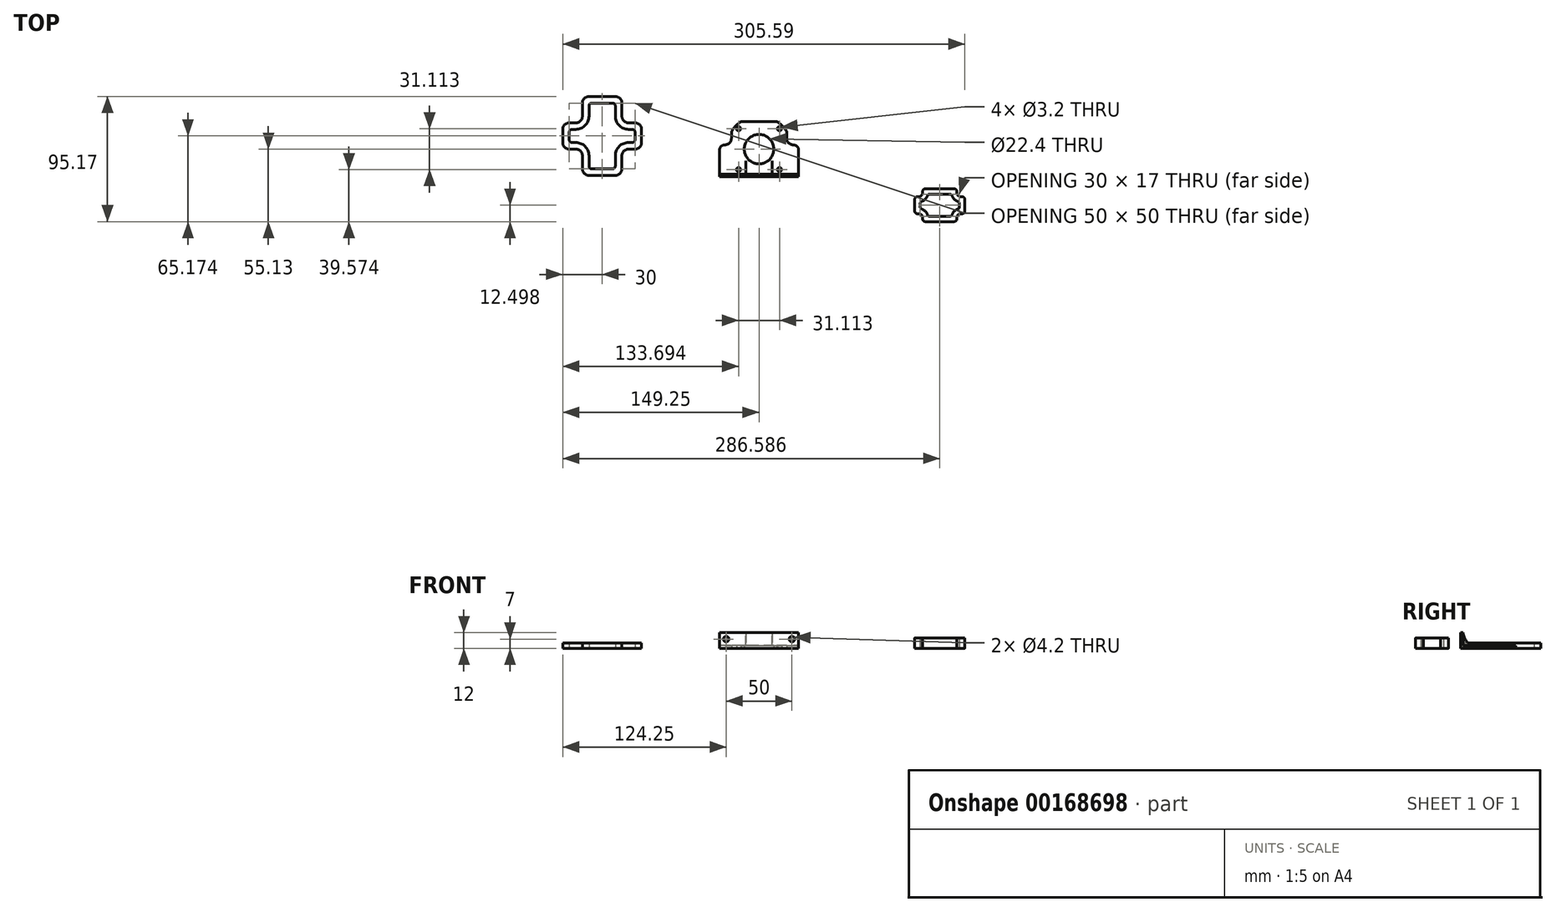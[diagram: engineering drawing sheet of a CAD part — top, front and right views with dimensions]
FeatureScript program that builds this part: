
annotation { "Feature Type Name" : "Feature", "Feature Type Description" : "" }
export const myFeature = defineFeature(function(context is Context, id is Id, definition is map)
    precondition{}
    {
        {
            var Q0;
            Q0=qCreatedBy(makeId("Top.planeOp"),FACE);
            var sketch = newSketch(context, id + "F0", { "sketchPlane" : qUnion([Q0])});
            skCircle(sketch, "E0", {"center": v(0, 0) * mm, "radius": 11.2 * mm});
            skLineSegment(sketch, "E1.bottom", {"start": v(-21, 21) * mm, "end": v(21, 21) * mm});
            skLineSegment(sketch, "E1.top", {"start": v(-21, -21) * mm, "end": v(21, -21) * mm});
            skLineSegment(sketch, "E1.left", {"start": v(-21, 21) * mm, "end": v(-21, 8.3) * mm});
            skLineSegment(sketch, "E1.right", {"start": v(21, 21) * mm, "end": v(21, 8.3) * mm});
            skLineSegment(sketch, "E2", {"start": v(-21, 21) * mm, "end": v(21, -21) * mm, "construction": true});
            skLineSegment(sketch, "E3", {"start": v(-21, -21) * mm, "end": v(21, 21) * mm, "construction": true});
            skCircle(sketch, "E4", {"center": v(0, 0) * mm, "radius": 22 * mm, "construction": true});
            skCircle(sketch, "E5", {"center": v(-15.56, 15.56) * mm, "radius": 1.6 * mm});
            skCircle(sketch, "E6", {"center": v(15.56, 15.56) * mm, "radius": 1.6 * mm});
            skCircle(sketch, "E7", {"center": v(-15.56, -15.56) * mm, "radius": 1.6 * mm});
            skCircle(sketch, "E8", {"center": v(15.56, -15.56) * mm, "radius": 1.6 * mm});
            skLineSegment(sketch, "E9.bottom", {"start": v(-30, -21) * mm, "end": v(30, -21) * mm});
            skLineSegment(sketch, "E9.top", {"start": v(-30, -19) * mm, "end": v(30, -19) * mm});
            skLineSegment(sketch, "E9.left", {"start": v(-30, -19) * mm, "end": v(-30, -21) * mm});
            skLineSegment(sketch, "E9.right", {"start": v(30, -19) * mm, "end": v(30, -21) * mm});
            skLineSegment(sketch, "E10.bottom", {"start": v(-30, -19) * mm, "end": v(-21, -19) * mm});
            skLineSegment(sketch, "E10.top", {"start": v(-26, 3.3) * mm, "end": v(-26, 3.3) * mm});
            skLineSegment(sketch, "E10.left", {"start": v(-30, -19) * mm, "end": v(-30, -0.7) * mm});
            skLineSegment(sketch, "E10.right", {"start": v(-21, -19) * mm, "end": v(-21, 0) * mm});
            skLineSegment(sketch, "E11.bottom", {"start": v(30, -19) * mm, "end": v(21, -19) * mm});
            skLineSegment(sketch, "E11.top", {"start": v(26, 3.3) * mm, "end": v(26, 3.3) * mm});
            skLineSegment(sketch, "E11.left", {"start": v(30, -19) * mm, "end": v(30, -0.7) * mm});
            skLineSegment(sketch, "E11.right", {"start": v(21, -19) * mm, "end": v(21, 0) * mm});
            skPoint(sketch, "E12.newPointA", {"position": v(-21, 3.3) * mm});
            skPoint(sketch, "E12.newPointB", {"position": v(-21, -14.42) * mm});
            skArc(sketch, "E12.filletArc", {"start": v(-26, 3.3) * mm, "mid": v(-22.46, 4.76) * mm, "end": v(-21, 8.3) * mm});
            skPoint(sketch, "E13.newPointA", {"position": v(21, 3.3) * mm});
            skPoint(sketch, "E13.newPointB", {"position": v(21, -14.42) * mm});
            skArc(sketch, "E13.filletArc", {"start": v(21, 8.3) * mm, "mid": v(22.46, 4.76) * mm, "end": v(26, 3.3) * mm});
            skPoint(sketch, "E14.visualSharp", {"position": v(-30, 3.3) * mm});
            skArc(sketch, "E14.filletArc", {"start": v(-26, 3.3) * mm, "mid": v(-28.83, 2.12) * mm, "end": v(-30, -0.7) * mm});
            skPoint(sketch, "E15.visualSharp", {"position": v(30, 3.3) * mm});
            skArc(sketch, "E15.filletArc", {"start": v(30, -0.7) * mm, "mid": v(28.83, 2.12) * mm, "end": v(26, 3.3) * mm});
            skArc(sketch, "E16", {"start": v(-21, 13.56) * mm, "mid": v(-17.68, 17.68) * mm, "end": v(-13.56, 21) * mm});
            skArc(sketch, "E17.MirrorCS", {"start": v(21, 13.56) * mm, "mid": v(17.68, 17.68) * mm, "end": v(13.56, 21) * mm});
            skSolve(sketch);
        }
        {
            var Q0;
            Q0=makeQuery(id+"F0.imprint","IMPRINT",FACE,{"disambiguationData":[TD([[makeQuery(id+"F0.imprint","IMPRINT",EDGE,{"derivedFrom":sQuery(id+"F0.wireOp",EDGE,"E0")}),-1.0]])]});
            extrude(context, id + "F1", {"entities" : qUnion([Q0]), "depth" : 2 * mm});
        }
        {
            var Q0;
            Q0=makeQuery(id+"F0.imprint","IMPRINT",FACE,{"disambiguationData":[TD([[makeQuery(id+"F0.imprint","IMPRINT",EDGE,{"derivedFrom":sQuery(id+"F0.wireOp",EDGE,"E9.top")}),-1.0]])]});
            extrude(context, id + "F2", {"entities" : qUnion([Q0]), "operationType" : NewBodyOperationType.ADD, "depth" : 12 * mm});
        }
        {
            var Q0;
            Q0=makeQuery(id+"F2.opExtrude","SWEPT_FACE",FACE,{"disambiguationData":[OSD([sQuery(id+"F0.wireOp",EDGE,"E9.top"),sQuery(id+"F0.wireOp",EDGE,"E10.bottom"),sQuery(id+"F0.wireOp",EDGE,"E11.bottom")])]});
            var sketch = newSketch(context, id + "F3", { "sketchPlane" : qUnion([Q0])});
            skLineSegment(sketch, "E18", {"start": v(20, 2) * mm, "end": v(20, 12) * mm});
            skCircle(sketch, "E19", {"center": v(25, 7) * mm, "radius": 2.1 * mm});
            skPoint(sketch, "E19.centerSnap0", {"position": v(20, 7) * mm});
            skCircle(sketch, "E20", {"center": v(-25, 7) * mm, "radius": 2.1 * mm});
            skSolve(sketch);
        }
        {
            var Q0;
            Q0=makeQuery(id+"F2.boolean.opBoolean","MERGE",FACE,{"derivedFrom":[makeQuery(id+"F1.opExtrude","SWEPT_FACE",FACE,{"disambiguationData":[OSD([sQuery(id+"F0.wireOp",EDGE,"E10.left")])]}),makeQuery(id+"F2.opExtrude","SWEPT_FACE",FACE,{"disambiguationData":[OSD([sQuery(id+"F0.wireOp",EDGE,"E9.left")])]})]});
            var sketch = newSketch(context, id + "F4", { "sketchPlane" : qUnion([Q0])});
            skLineSegment(sketch, "E21", {"start": v(0.7, 2) * mm, "end": v(9, 2) * mm});
            skLineSegment(sketch, "E22", {"start": v(19, 12) * mm, "end": v(19, 12) * mm});
            skPoint(sketch, "E23.visualSharp", {"position": v(19, 2) * mm});
            skArc(sketch, "E23.filletArc", {"start": v(9, 2) * mm, "mid": v(16.07, 4.93) * mm, "end": v(19, 12) * mm});
            skSolve(sketch);
        }
        {
            var Q0;
            Q0 = qSketchRegion(id + "F4", true);
            var Q1;
            {var subQ0=sQuery(id+"F4.wireOp",EDGE,"E23.filletArc");Q1=makeQuery(id+"F4.imprint","IMPRINT",FACE,{"disambiguationData":[TD([[makeQuery(id+"F4.imprint","IMPRINT",EDGE,{"derivedFrom":subQ0}),-1.0]])]});}
            extrude(context, id + "F5", {"entities" : qUnion([Q0, Q1]), "operationType" : NewBodyOperationType.ADD, "oppositeDirection" : true, "depth" : 40 * mm});
        }
        {
            var Q0;
            {var subQ0=sQuery(id+"F4.wireOp",EDGE,"E23.filletArc");Q0=makeQuery(id+"F4.imprint","IMPRINT",FACE,{"disambiguationData":[TD([[makeQuery(id+"F4.imprint","IMPRINT",EDGE,{"derivedFrom":subQ0}),-1.0]])]});}
            extrude(context, id + "F6", {"entities" : qUnion([Q0]), "operationType" : NewBodyOperationType.REMOVE, "oppositeDirection" : true, "depth" : 20 * mm});
        }
        {
            var Q0;
            Q0=makeQuery(id+"F3.imprint","IMPRINT",FACE,{"disambiguationData":[TD([[makeQuery(id+"F3.imprint","IMPRINT",EDGE,{"derivedFrom":sQuery(id+"F3.wireOp",EDGE,"E20")}),1.0]])]});
            var Q1;
            Q1=makeQuery(id+"F3.imprint","IMPRINT",FACE,{"disambiguationData":[TD([[makeQuery(id+"F3.imprint","IMPRINT",EDGE,{"derivedFrom":sQuery(id+"F3.wireOp",EDGE,"E19")}),1.0]])]});
            extrude(context, id + "F7", {"entities" : qUnion([Q0, Q1]), "operationType" : NewBodyOperationType.REMOVE, "oppositeDirection" : true, "depth" : 25 * mm});
        }
        {
            var Q0;
            Q0=makeQuery(id+"F0.imprint","IMPRINT",FACE,{"disambiguationData":[TD([[makeQuery(id+"F0.imprint","IMPRINT",EDGE,{"derivedFrom":sQuery(id+"F0.wireOp",EDGE,"E0")}),1.0]])]});
            extrude(context, id + "F8", {"entities" : qUnion([Q0]), "operationType" : NewBodyOperationType.REMOVE, "depth" : 25 * mm});
        }
        {
            var Q0;
            Q0=makeQuery(id+"F1.opExtrude","CAP_EDGE",EDGE,{"disambiguationData":[OSD([sQuery(id+"F0.wireOp",EDGE,"E9.top"),sQuery(id+"F0.wireOp",EDGE,"E10.bottom"),sQuery(id+"F0.wireOp",EDGE,"E11.bottom")])],"isStart":false});
            var Q1;
            Q1=makeQuery(id+"F6.boolean.opBoolean","COPY",EDGE,{"derivedFrom":makeQuery(id+"F6.opExtrude","SWEPT_EDGE",EDGE,{"disambiguationData":[OSD([sQuery(id+"F0.wireOp",EDGE,"E9.left"),sQuery(id+"F0.wireOp",EDGE,"E10.bottom"),sQuery(id+"F0.wireOp",EDGE,"E10.left")])]})});
            fillet(context, id + "F9", {"entities" : qUnion([Q0, Q1]), "radius" : 1 * mm, "tangentPropagation" : true, "allowEdgeOverflow" : false});
        }
        {
            var Q0;
            Q0=qCreatedBy(makeId("Top.planeOp"),FACE);
            var sketch = newSketch(context, id + "F10", { "sketchPlane" : qUnion([Q0])});
            skLineSegment(sketch, "E24.bottom", {"start": v(-109.25, -19.96) * mm, "end": v(-129.25, -19.96) * mm});
            skLineSegment(sketch, "E24.top", {"start": v(-109.25, 40.04) * mm, "end": v(-129.25, 40.04) * mm});
            skLineSegment(sketch, "E24.left", {"start": v(-89.25, 5.04) * mm, "end": v(-89.25, 15.04) * mm});
            skLineSegment(sketch, "E24.right", {"start": v(-149.25, 5.04) * mm, "end": v(-149.25, 15.04) * mm});
            skPoint(sketch, "E24.middle", {"position": v(-119.25, 10.04) * mm});
            skLineSegment(sketch, "E25.0", {"start": v(-139.25, 20.04) * mm, "end": v(-144.25, 20.04) * mm});
            skLineSegment(sketch, "E26.0", {"start": v(-139.25, 0.04) * mm, "end": v(-144.25, 0.04) * mm});
            skLineSegment(sketch, "E27.0", {"start": v(-134.25, -14.96) * mm, "end": v(-134.25, -4.96) * mm});
            skLineSegment(sketch, "E28.0", {"start": v(-104.25, -14.96) * mm, "end": v(-104.25, -4.96) * mm});
            skArc(sketch, "E29.filletArc", {"start": v(-144.25, 20.04) * mm, "mid": v(-147.79, 18.58) * mm, "end": v(-149.25, 15.04) * mm});
            skArc(sketch, "E30.filletArc", {"start": v(-149.25, 5.04) * mm, "mid": v(-147.79, 1.5) * mm, "end": v(-144.25, 0.04) * mm});
            skArc(sketch, "E31.filletArc", {"start": v(-134.25, -4.96) * mm, "mid": v(-135.71, -1.42) * mm, "end": v(-139.25, 0.04) * mm});
            skPoint(sketch, "E32.newPointB", {"position": v(-149.25, -19.96) * mm});
            skArc(sketch, "E32.filletArc", {"start": v(-134.25, -14.96) * mm, "mid": v(-132.79, -18.5) * mm, "end": v(-129.25, -19.96) * mm});
            skPoint(sketch, "E33.newPointA", {"position": v(-89.25, -19.96) * mm});
            skArc(sketch, "E33.filletArc", {"start": v(-109.25, -19.96) * mm, "mid": v(-105.71, -18.5) * mm, "end": v(-104.25, -14.96) * mm});
            skLineSegment(sketch, "E34", {"start": v(-134.25, 35.04) * mm, "end": v(-134.25, 25.04) * mm});
            skPoint(sketch, "E34.startSnap0", {"position": v(-119.25, 40.04) * mm});
            skLineSegment(sketch, "E35", {"start": v(-94.25, 0.04) * mm, "end": v(-99.25, 0.04) * mm});
            skArc(sketch, "E36.filletArc", {"start": v(-139.25, 20.04) * mm, "mid": v(-135.71, 21.5) * mm, "end": v(-134.25, 25.04) * mm});
            skPoint(sketch, "E37.newPointB", {"position": v(-89.25, 40.04) * mm});
            skArc(sketch, "E37.filletArc", {"start": v(-104.25, 35.04) * mm, "mid": v(-105.71, 38.58) * mm, "end": v(-109.25, 40.04) * mm});
            skPoint(sketch, "E38.newPointA", {"position": v(-134.25, 40.04) * mm});
            skPoint(sketch, "E38.newPointB", {"position": v(-149.25, 40.04) * mm});
            skArc(sketch, "E38.filletArc", {"start": v(-129.25, 40.04) * mm, "mid": v(-132.79, 38.58) * mm, "end": v(-134.25, 35.04) * mm});
            skPoint(sketch, "E39.newPointA", {"position": v(-89.25, 0.04) * mm});
            skArc(sketch, "E39.filletArc", {"start": v(-94.25, 0.04) * mm, "mid": v(-90.71, 1.5) * mm, "end": v(-89.25, 5.04) * mm});
            skArc(sketch, "E40.filletArc", {"start": v(-99.25, 0.04) * mm, "mid": v(-102.79, -1.42) * mm, "end": v(-104.25, -4.96) * mm});
            skLineSegment(sketch, "E41", {"start": v(-104.25, 35.04) * mm, "end": v(-104.25, 25.04) * mm});
            skLineSegment(sketch, "E42", {"start": v(-94.25, 20.04) * mm, "end": v(-99.25, 20.04) * mm});
            skArc(sketch, "E43.filletArc", {"start": v(-104.25, 25.04) * mm, "mid": v(-102.79, 21.5) * mm, "end": v(-99.25, 20.04) * mm});
            skPoint(sketch, "E44.newPointB", {"position": v(-89.25, 20.04) * mm});
            skArc(sketch, "E44.filletArc", {"start": v(-89.25, 15.04) * mm, "mid": v(-90.71, 18.58) * mm, "end": v(-94.25, 20.04) * mm});
            skLineSegment(sketch, "E45", {"start": v(-129.25, 33.04) * mm, "end": v(-129.25, 25.04) * mm});
            skLineSegment(sketch, "E46", {"start": v(-139.25, 15.04) * mm, "end": v(-142.25, 15.04) * mm});
            skLineSegment(sketch, "E47", {"start": v(-144.25, 13.04) * mm, "end": v(-144.25, 7.04) * mm});
            skLineSegment(sketch, "E48", {"start": v(-139.25, 5.04) * mm, "end": v(-142.25, 5.04) * mm});
            skLineSegment(sketch, "E49", {"start": v(-129.25, -4.96) * mm, "end": v(-129.25, -12.96) * mm});
            skLineSegment(sketch, "E50", {"start": v(-127.25, -14.96) * mm, "end": v(-111.25, -14.96) * mm});
            skLineSegment(sketch, "E51", {"start": v(-109.25, -4.96) * mm, "end": v(-109.25, -12.96) * mm});
            skLineSegment(sketch, "E52", {"start": v(-99.25, 5.04) * mm, "end": v(-96.25, 5.04) * mm});
            skLineSegment(sketch, "E53", {"start": v(-94.25, 13.04) * mm, "end": v(-94.25, 7.04) * mm});
            skLineSegment(sketch, "E54", {"start": v(-96.25, 15.04) * mm, "end": v(-99.25, 15.04) * mm});
            skLineSegment(sketch, "E55", {"start": v(-109.25, 25.04) * mm, "end": v(-109.25, 33.04) * mm});
            skLineSegment(sketch, "E56", {"start": v(-127.25, 35.04) * mm, "end": v(-111.25, 35.04) * mm});
            skPoint(sketch, "E57.visualSharp", {"position": v(-129.25, 15.04) * mm});
            skArc(sketch, "E57.filletArc", {"start": v(-139.25, 15.04) * mm, "mid": v(-132.18, 17.97) * mm, "end": v(-129.25, 25.04) * mm});
            skPoint(sketch, "E58.visualSharp", {"position": v(-129.25, 5.04) * mm});
            skArc(sketch, "E58.filletArc", {"start": v(-129.25, -4.96) * mm, "mid": v(-132.18, 2.12) * mm, "end": v(-139.25, 5.04) * mm});
            skPoint(sketch, "E59.visualSharp", {"position": v(-109.25, 5.04) * mm});
            skArc(sketch, "E59.filletArc", {"start": v(-99.25, 5.04) * mm, "mid": v(-106.32, 2.12) * mm, "end": v(-109.25, -4.96) * mm});
            skPoint(sketch, "E60.visualSharp", {"position": v(-109.25, 15.04) * mm});
            skArc(sketch, "E60.filletArc", {"start": v(-109.25, 25.04) * mm, "mid": v(-106.32, 17.97) * mm, "end": v(-99.25, 15.04) * mm});
            skArc(sketch, "E61.filletArc", {"start": v(-127.25, 35.04) * mm, "mid": v(-128.66, 34.46) * mm, "end": v(-129.25, 33.04) * mm});
            skArc(sketch, "E62.filletArc", {"start": v(-109.25, 33.04) * mm, "mid": v(-109.84, 34.46) * mm, "end": v(-111.25, 35.04) * mm});
            skArc(sketch, "E63.filletArc", {"start": v(-94.25, 13.04) * mm, "mid": v(-94.84, 14.46) * mm, "end": v(-96.25, 15.04) * mm});
            skArc(sketch, "E64.filletArc", {"start": v(-96.25, 5.04) * mm, "mid": v(-94.84, 5.63) * mm, "end": v(-94.25, 7.04) * mm});
            skArc(sketch, "E65.filletArc", {"start": v(-129.25, -12.96) * mm, "mid": v(-128.66, -14.37) * mm, "end": v(-127.25, -14.96) * mm});
            skArc(sketch, "E66.filletArc", {"start": v(-111.25, -14.96) * mm, "mid": v(-109.84, -14.37) * mm, "end": v(-109.25, -12.96) * mm});
            skArc(sketch, "E67.filletArc", {"start": v(-144.25, 7.04) * mm, "mid": v(-143.66, 5.63) * mm, "end": v(-142.25, 5.04) * mm});
            skArc(sketch, "E68.filletArc", {"start": v(-142.25, 15.04) * mm, "mid": v(-143.66, 14.46) * mm, "end": v(-144.25, 13.04) * mm});
            skLineSegment(sketch, "E69.bottom", {"start": v(121.34, -33.13) * mm, "end": v(153.34, -33.13) * mm, "construction": true});
            skLineSegment(sketch, "E69.top", {"start": v(121.34, -52.13) * mm, "end": v(153.34, -52.13) * mm, "construction": true});
            skLineSegment(sketch, "E69.left", {"start": v(121.34, -33.13) * mm, "end": v(121.34, -52.13) * mm, "construction": true});
            skLineSegment(sketch, "E69.right", {"start": v(153.34, -33.13) * mm, "end": v(153.34, -52.13) * mm, "construction": true});
            skCircle(sketch, "E70", {"center": v(121.34, -33.13) * mm, "radius": 3 * mm});
            skCircle(sketch, "E71", {"center": v(121.34, -52.13) * mm, "radius": 3 * mm});
            skCircle(sketch, "E72", {"center": v(153.34, -33.13) * mm, "radius": 3 * mm});
            skCircle(sketch, "E73", {"center": v(153.34, -52.13) * mm, "radius": 3 * mm});
            skLineSegment(sketch, "E74", {"start": v(118.34, -33.13) * mm, "end": v(118.34, -52.13) * mm});
            skLineSegment(sketch, "E75", {"start": v(121.34, -55.13) * mm, "end": v(153.34, -55.13) * mm});
            skLineSegment(sketch, "E76", {"start": v(156.34, -52.13) * mm, "end": v(156.34, -33.13) * mm});
            skLineSegment(sketch, "E77", {"start": v(153.34, -30.13) * mm, "end": v(121.34, -30.13) * mm});
            skLineSegment(sketch, "E78", {"start": v(121.34, -36.13) * mm, "end": v(118.34, -36.13) * mm});
            skLineSegment(sketch, "E79", {"start": v(121.34, -49.13) * mm, "end": v(118.34, -49.13) * mm});
            skLineSegment(sketch, "E80", {"start": v(124.34, -52.13) * mm, "end": v(124.34, -55.13) * mm});
            skLineSegment(sketch, "E81", {"start": v(150.34, -52.13) * mm, "end": v(150.34, -55.13) * mm});
            skLineSegment(sketch, "E82", {"start": v(153.34, -49.13) * mm, "end": v(156.34, -49.13) * mm});
            skLineSegment(sketch, "E83", {"start": v(153.34, -36.13) * mm, "end": v(156.34, -36.13) * mm});
            skLineSegment(sketch, "E84", {"start": v(150.34, -33.13) * mm, "end": v(150.34, -30.13) * mm});
            skCircle(sketch, "E85", {"center": v(121.34, -52.13) * mm, "radius": 7 * mm});
            skCircle(sketch, "E86", {"center": v(121.34, -33.13) * mm, "radius": 7 * mm});
            skCircle(sketch, "E87", {"center": v(153.34, -33.13) * mm, "radius": 7 * mm});
            skCircle(sketch, "E88", {"center": v(153.34, -52.13) * mm, "radius": 7 * mm});
            skLineSegment(sketch, "E89.0", {"start": v(122.34, -33.13) * mm, "end": v(122.34, -52.13) * mm});
            skLineSegment(sketch, "E90.0", {"start": v(152.34, -52.13) * mm, "end": v(152.34, -33.13) * mm});
            skLineSegment(sketch, "E91.0", {"start": v(153.34, -34.13) * mm, "end": v(121.34, -34.13) * mm});
            skLineSegment(sketch, "E92.0", {"start": v(121.34, -51.13) * mm, "end": v(153.34, -51.13) * mm});
            skLineSegment(sketch, "E93", {"start": v(124.34, -33.13) * mm, "end": v(124.34, -30.13) * mm});
            skSolve(sketch);
        }
        {
            var Q0;
            Q0=makeQuery(id+"F10.imprint","IMPRINT",FACE,{"disambiguationData":[TD([[makeQuery(id+"F10.imprint","IMPRINT",EDGE,{"derivedFrom":sQuery(id+"F10.wireOp",EDGE,"E24.bottom")}),-1.0]])]});
            extrude(context, id + "F11", {"entities" : qUnion([Q0]), "depth" : 4 * mm});
        }
        {
            var Q0;
            {var subQ5=sQuery(id+"F10.wireOp",EDGE,"E78");Q0=makeQuery(id+"F10.imprint","IMPRINT",FACE,{"disambiguationData":[TD([[makeQuery(id+"F10.imprint","IMPRINT",EDGE,{"derivedFrom":subQ5}),1.0]])]});}
            var Q1;
            {var subQ0=sQuery(id+"F10.wireOp",EDGE,"E86");var subQ1=sQuery(id+"F10.wireOp",EDGE,"E74");var subQ2=makeQuery(id+"F10.imprint","INTERSECT",VERTEX,{"derivedFrom":[subQ1,subQ0]});Q1=makeQuery(id+"F10.imprint","IMPRINT",FACE,{"disambiguationData":[TD([[makeQuery(id+"F10.imprint","IMPRINT",EDGE,{"disambiguationData":[TD([[subQ2,-1.0]])],"derivedFrom":subQ1}),1.0]])]});}
            var Q2;
            {var subQ0=sQuery(id+"F10.wireOp",EDGE,"E79");Q2=makeQuery(id+"F10.imprint","IMPRINT",FACE,{"disambiguationData":[TD([[makeQuery(id+"F10.imprint","IMPRINT",EDGE,{"derivedFrom":subQ0}),-1.0]])]});}
            var Q3;
            {var subQ0=sQuery(id+"F10.wireOp",EDGE,"E92.0");var subQ1=sQuery(id+"F10.wireOp",EDGE,"E71");var subQ2=makeQuery(id+"F10.imprint","INTERSECT",VERTEX,{"derivedFrom":[subQ1,subQ0]});Q3=makeQuery(id+"F10.imprint","IMPRINT",FACE,{"disambiguationData":[TD([[makeQuery(id+"F10.imprint","IMPRINT",EDGE,{"disambiguationData":[TD([[subQ2,-1.0]])],"derivedFrom":subQ1}),-1.0]])]});}
            var Q4;
            {var subQ5=sQuery(id+"F10.wireOp",EDGE,"E80");Q4=makeQuery(id+"F10.imprint","IMPRINT",FACE,{"disambiguationData":[TD([[makeQuery(id+"F10.imprint","IMPRINT",EDGE,{"derivedFrom":subQ5}),1.0]])]});}
            var Q5;
            {var subQ0=sQuery(id+"F10.wireOp",EDGE,"E85");var subQ1=sQuery(id+"F10.wireOp",EDGE,"E75");var subQ2=makeQuery(id+"F10.imprint","INTERSECT",VERTEX,{"derivedFrom":[subQ1,subQ0]});Q5=makeQuery(id+"F10.imprint","IMPRINT",FACE,{"disambiguationData":[TD([[makeQuery(id+"F10.imprint","IMPRINT",EDGE,{"disambiguationData":[TD([[subQ2,-1.0]])],"derivedFrom":subQ1}),1.0]])]});}
            var Q6;
            {var subQ5=sQuery(id+"F10.wireOp",EDGE,"E81");Q6=makeQuery(id+"F10.imprint","IMPRINT",FACE,{"disambiguationData":[TD([[makeQuery(id+"F10.imprint","IMPRINT",EDGE,{"derivedFrom":subQ5}),-1.0]])]});}
            var Q7;
            {var subQ0=sQuery(id+"F10.wireOp",EDGE,"E90.0");var subQ1=sQuery(id+"F10.wireOp",EDGE,"E73");var subQ2=makeQuery(id+"F10.imprint","INTERSECT",VERTEX,{"derivedFrom":[subQ1,subQ0]});Q7=makeQuery(id+"F10.imprint","IMPRINT",FACE,{"disambiguationData":[TD([[makeQuery(id+"F10.imprint","IMPRINT",EDGE,{"disambiguationData":[TD([[subQ2,-1.0]])],"derivedFrom":subQ1}),-1.0]])]});}
            var Q8;
            {var subQ5=sQuery(id+"F10.wireOp",EDGE,"E82");Q8=makeQuery(id+"F10.imprint","IMPRINT",FACE,{"disambiguationData":[TD([[makeQuery(id+"F10.imprint","IMPRINT",EDGE,{"derivedFrom":subQ5}),1.0]])]});}
            var Q9;
            {var subQ0=sQuery(id+"F10.wireOp",EDGE,"E88");var subQ1=sQuery(id+"F10.wireOp",EDGE,"E76");var subQ2=makeQuery(id+"F10.imprint","INTERSECT",VERTEX,{"derivedFrom":[subQ1,subQ0]});Q9=makeQuery(id+"F10.imprint","IMPRINT",FACE,{"disambiguationData":[TD([[makeQuery(id+"F10.imprint","IMPRINT",EDGE,{"disambiguationData":[TD([[subQ2,-1.0]])],"derivedFrom":subQ1}),1.0]])]});}
            var Q10;
            {var subQ0=sQuery(id+"F10.wireOp",EDGE,"E83");Q10=makeQuery(id+"F10.imprint","IMPRINT",FACE,{"disambiguationData":[TD([[makeQuery(id+"F10.imprint","IMPRINT",EDGE,{"derivedFrom":subQ0}),-1.0]])]});}
            var Q11;
            {var subQ0=sQuery(id+"F10.wireOp",EDGE,"E91.0");var subQ1=sQuery(id+"F10.wireOp",EDGE,"E72");var subQ2=makeQuery(id+"F10.imprint","INTERSECT",VERTEX,{"derivedFrom":[subQ1,subQ0]});Q11=makeQuery(id+"F10.imprint","IMPRINT",FACE,{"disambiguationData":[TD([[makeQuery(id+"F10.imprint","IMPRINT",EDGE,{"disambiguationData":[TD([[subQ2,-1.0]])],"derivedFrom":subQ1}),-1.0]])]});}
            var Q12;
            {var subQ0=sQuery(id+"F10.wireOp",EDGE,"E84");Q12=makeQuery(id+"F10.imprint","IMPRINT",FACE,{"disambiguationData":[TD([[makeQuery(id+"F10.imprint","IMPRINT",EDGE,{"derivedFrom":subQ0}),1.0]])]});}
            var Q13;
            {var subQ0=sQuery(id+"F10.wireOp",EDGE,"E87");var subQ1=sQuery(id+"F10.wireOp",EDGE,"E77");var subQ2=makeQuery(id+"F10.imprint","INTERSECT",VERTEX,{"derivedFrom":[subQ1,subQ0]});Q13=makeQuery(id+"F10.imprint","IMPRINT",FACE,{"disambiguationData":[TD([[makeQuery(id+"F10.imprint","IMPRINT",EDGE,{"disambiguationData":[TD([[subQ2,-1.0]])],"derivedFrom":subQ1}),1.0]])]});}
            var Q14;
            {var subQ7=sQuery(id+"F10.wireOp",EDGE,"E93");Q14=makeQuery(id+"F10.imprint","IMPRINT",FACE,{"disambiguationData":[TD([[makeQuery(id+"F10.imprint","IMPRINT",EDGE,{"derivedFrom":subQ7}),-1.0]])]});}
            var Q15;
            {var subQ0=sQuery(id+"F10.wireOp",EDGE,"E89.0");var subQ1=sQuery(id+"F10.wireOp",EDGE,"E70");var subQ2=makeQuery(id+"F10.imprint","INTERSECT",VERTEX,{"derivedFrom":[subQ1,subQ0]});Q15=makeQuery(id+"F10.imprint","IMPRINT",FACE,{"disambiguationData":[TD([[makeQuery(id+"F10.imprint","IMPRINT",EDGE,{"disambiguationData":[TD([[subQ2,-1.0]])],"derivedFrom":subQ1}),-1.0]])]});}
            extrude(context, id + "F12", {"entities" : qUnion([Q0, Q1, Q2, Q3, Q4, Q5, Q6, Q7, Q8, Q9, Q10, Q11, Q12, Q13, Q14, Q15]), "depth" : 8 * mm, "offsetDistance" : 25 * mm});
        }
        {
            var Q0;
            Q0=makeQuery(id+"F12.opExtrude","SWEPT_EDGE",EDGE,{"disambiguationData":[OSD([sQuery(id+"F10.wireOp",EDGE,"E86"),sQuery(id+"F10.wireOp",EDGE,"E89.0")])]});
            var Q1;
            Q1=makeQuery(id+"F12.opExtrude","SWEPT_EDGE",EDGE,{"disambiguationData":[OSD([sQuery(id+"F10.wireOp",EDGE,"E86"),sQuery(id+"F10.wireOp",EDGE,"E91.0")])]});
            var Q2;
            Q2=makeQuery(id+"F12.opExtrude","SWEPT_EDGE",EDGE,{"disambiguationData":[OSD([sQuery(id+"F10.wireOp",EDGE,"E75"),sQuery(id+"F10.wireOp",EDGE,"E81")])]});
            var Q3;
            Q3=makeQuery(id+"F12.opExtrude","SWEPT_EDGE",EDGE,{"disambiguationData":[OSD([sQuery(id+"F10.wireOp",EDGE,"E76"),sQuery(id+"F10.wireOp",EDGE,"E82")])]});
            var Q4;
            Q4=makeQuery(id+"F12.opExtrude","SWEPT_EDGE",EDGE,{"disambiguationData":[OSD([sQuery(id+"F10.wireOp",EDGE,"E75"),sQuery(id+"F10.wireOp",EDGE,"E80")])]});
            var Q5;
            Q5=makeQuery(id+"F12.opExtrude","SWEPT_EDGE",EDGE,{"disambiguationData":[OSD([sQuery(id+"F10.wireOp",EDGE,"E74"),sQuery(id+"F10.wireOp",EDGE,"E79")])]});
            var Q6;
            Q6=makeQuery(id+"F12.opExtrude","SWEPT_EDGE",EDGE,{"disambiguationData":[OSD([sQuery(id+"F10.wireOp",EDGE,"E85"),sQuery(id+"F10.wireOp",EDGE,"E89.0")])]});
            var Q7;
            Q7=makeQuery(id+"F12.opExtrude","SWEPT_EDGE",EDGE,{"disambiguationData":[OSD([sQuery(id+"F10.wireOp",EDGE,"E85"),sQuery(id+"F10.wireOp",EDGE,"E92.0")])]});
            var Q8;
            Q8=makeQuery(id+"F12.opExtrude","SWEPT_EDGE",EDGE,{"disambiguationData":[OSD([sQuery(id+"F10.wireOp",EDGE,"E88"),sQuery(id+"F10.wireOp",EDGE,"E92.0")])]});
            var Q9;
            Q9=makeQuery(id+"F12.opExtrude","SWEPT_EDGE",EDGE,{"disambiguationData":[OSD([sQuery(id+"F10.wireOp",EDGE,"E88"),sQuery(id+"F10.wireOp",EDGE,"E90.0")])]});
            var Q10;
            Q10=makeQuery(id+"F12.opExtrude","SWEPT_EDGE",EDGE,{"disambiguationData":[OSD([sQuery(id+"F10.wireOp",EDGE,"E87"),sQuery(id+"F10.wireOp",EDGE,"E90.0")])]});
            var Q11;
            Q11=makeQuery(id+"F12.opExtrude","SWEPT_EDGE",EDGE,{"disambiguationData":[OSD([sQuery(id+"F10.wireOp",EDGE,"E87"),sQuery(id+"F10.wireOp",EDGE,"E91.0")])]});
            var Q12;
            Q12=makeQuery(id+"F12.opExtrude","SWEPT_EDGE",EDGE,{"disambiguationData":[OSD([sQuery(id+"F10.wireOp",EDGE,"E74"),sQuery(id+"F10.wireOp",EDGE,"E78")])]});
            var Q13;
            Q13=makeQuery(id+"F12.opExtrude","SWEPT_EDGE",EDGE,{"disambiguationData":[OSD([sQuery(id+"F10.wireOp",EDGE,"E77"),sQuery(id+"F10.wireOp",EDGE,"E93")])]});
            var Q14;
            Q14=makeQuery(id+"F12.opExtrude","SWEPT_EDGE",EDGE,{"disambiguationData":[OSD([sQuery(id+"F10.wireOp",EDGE,"E77"),sQuery(id+"F10.wireOp",EDGE,"E84")])]});
            var Q15;
            Q15=makeQuery(id+"F12.opExtrude","SWEPT_EDGE",EDGE,{"disambiguationData":[OSD([sQuery(id+"F10.wireOp",EDGE,"E76"),sQuery(id+"F10.wireOp",EDGE,"E83")])]});
            fillet(context, id + "F13", {"entities" : qUnion([Q0, Q1, Q2, Q3, Q4, Q5, Q6, Q7, Q8, Q9, Q10, Q11, Q12, Q13, Q14, Q15]), "radius" : 2 * mm, "tangentPropagation" : true, "allowEdgeOverflow" : false});
        }
    });
